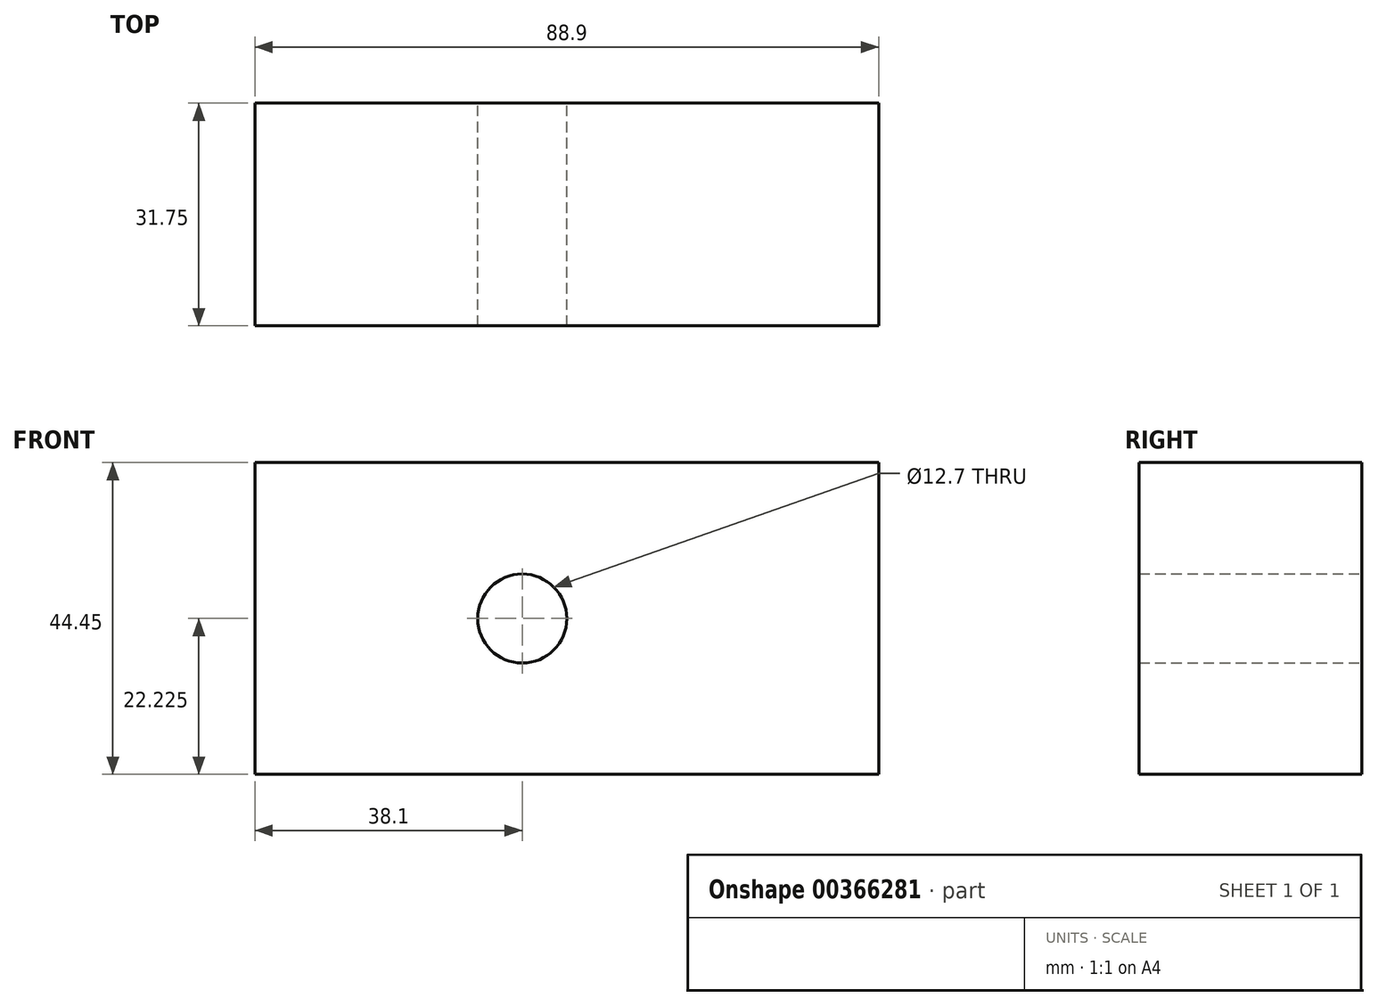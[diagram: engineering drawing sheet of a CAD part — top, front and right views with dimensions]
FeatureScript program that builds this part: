
annotation { "Feature Type Name" : "Feature", "Feature Type Description" : "" }
export const myFeature = defineFeature(function(context is Context, id is Id, definition is map)
    precondition{}
    {
        {
            var Q0;
            Q0=qCreatedBy(makeId("Front.planeOp"),FACE);
            var sketch = newSketch(context, id + "F0", { "sketchPlane" : qUnion([Q0])});
            skLineSegment(sketch, "E0", {"start": v(0, 0) * mm, "end": v(88.9, 0) * mm});
            skLineSegment(sketch, "E1", {"start": v(0, 44.45) * mm, "end": v(88.9, 44.45) * mm});
            skLineSegment(sketch, "E2", {"start": v(88.9, 44.45) * mm, "end": v(88.9, 0) * mm});
            skCircle(sketch, "E3", {"center": v(38.1, 22.22) * mm, "radius": 6.35 * mm});
            skLineSegment(sketch, "E4", {"start": v(0, 44.45) * mm, "end": v(0, 0) * mm});
            skSolve(sketch);
        }
        {
            var Q0;
            Q0=makeQuery(id+"F0.imprint","IMPRINT",FACE,{"disambiguationData":[TD([[makeQuery(id+"F0.imprint","IMPRINT",EDGE,{"derivedFrom":sQuery(id+"F0.wireOp",EDGE,"E0")}),1.0]])]});
            extrude(context, id + "F1", {"entities" : qUnion([Q0]), "depth" : 31.75 * mm});
        }
    });
